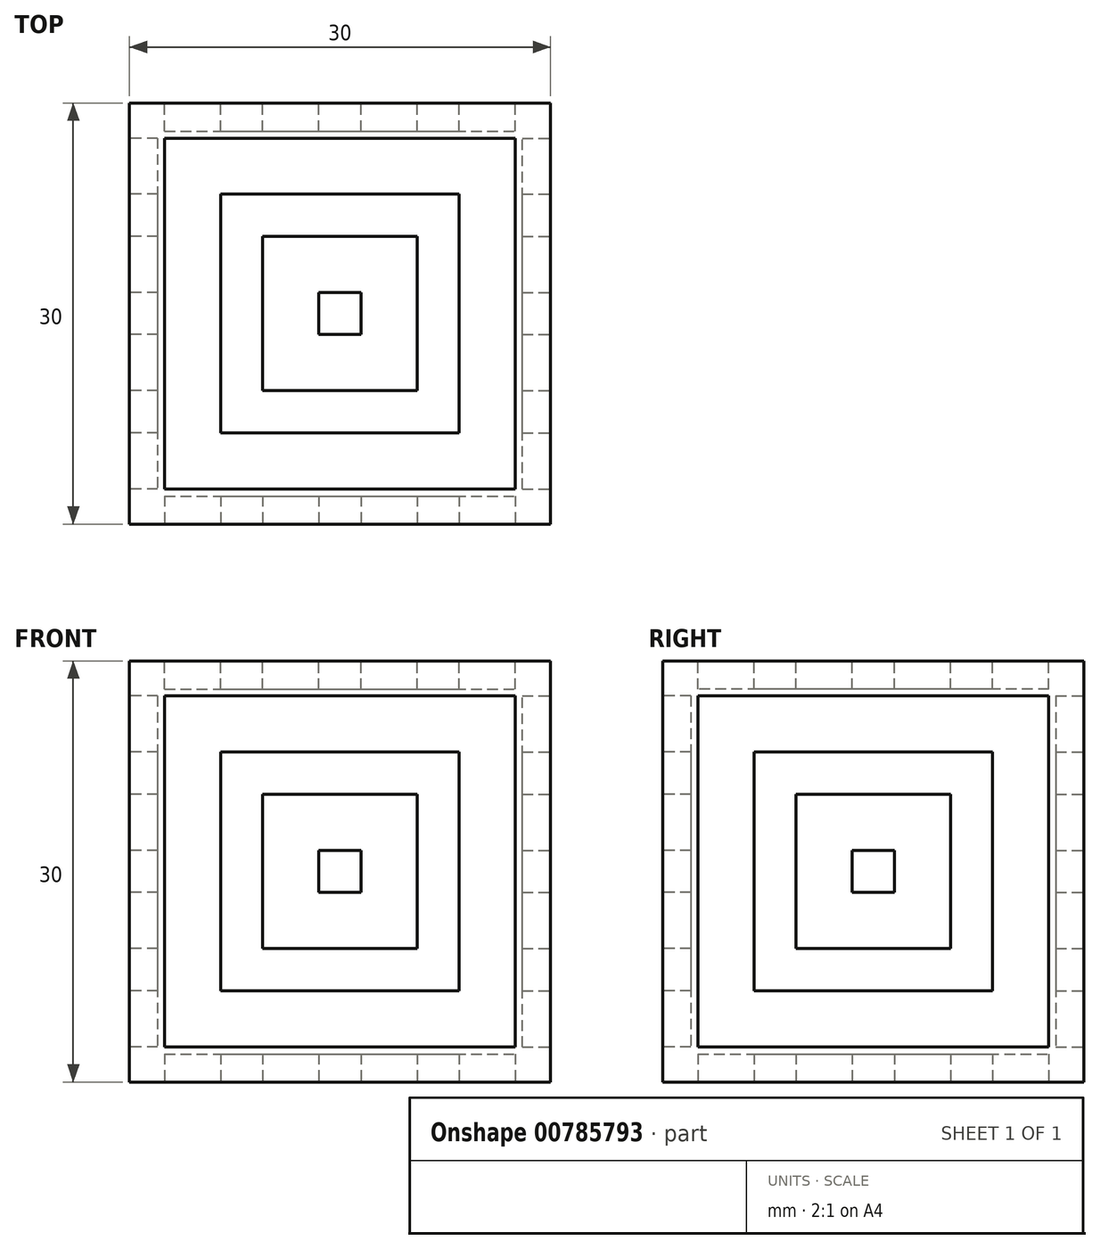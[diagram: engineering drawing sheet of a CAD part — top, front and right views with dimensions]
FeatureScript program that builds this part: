
annotation { "Feature Type Name" : "Feature", "Feature Type Description" : "" }
export const myFeature = defineFeature(function(context is Context, id is Id, definition is map)
    precondition{}
    {
        {
            var Q0;
            Q0=qCreatedBy(makeId("Front.planeOp"),FACE);
            var sketch = newSketch(context, id + "F0", { "sketchPlane" : qUnion([Q0])});
            skLineSegment(sketch, "E0.bottom", {"start": v(-15, 15) * mm, "end": v(15, 15) * mm});
            skLineSegment(sketch, "E0.top", {"start": v(-15, -15) * mm, "end": v(15, -15) * mm});
            skLineSegment(sketch, "E0.left", {"start": v(-15, 15) * mm, "end": v(-15, -15) * mm});
            skLineSegment(sketch, "E0.right", {"start": v(15, 15) * mm, "end": v(15, -15) * mm});
            skLineSegment(sketch, "E1", {"start": v(0, -15) * mm, "end": v(0, 15) * mm, "construction": true});
            skSolve(sketch);
        }
        {
            var Q0;
            Q0=makeQuery(id+"F0.imprint","IMPRINT",FACE,{"disambiguationData":[TD([[makeQuery(id+"F0.imprint","IMPRINT",EDGE,{"derivedFrom":sQuery(id+"F0.wireOp",EDGE,"E0.bottom")}),-1.0]])]});
            extrude(context, id + "F1", {"entities" : qUnion([Q0]), "depth" : 30 * mm, "offsetDistance" : 25 * mm});
        }
        {
            var Q0;
            Q0=makeQuery(id+"F1.opExtrude","SWEPT_FACE",FACE,{"disambiguationData":[OSD([sQuery(id+"F0.wireOp",EDGE,"E0.bottom")])]});
            var sketch = newSketch(context, id + "F2", { "sketchPlane" : qUnion([Q0])});
            skLineSegment(sketch, "E2", {"start": v(-15, -15) * mm, "end": v(15, -15) * mm, "construction": true});
            skLineSegment(sketch, "E3.bottom", {"start": v(-12.5, -2.5) * mm, "end": v(12.5, -2.5) * mm});
            skLineSegment(sketch, "E3.top", {"start": v(-12.5, -27.5) * mm, "end": v(12.5, -27.5) * mm});
            skLineSegment(sketch, "E3.left", {"start": v(-12.5, -2.5) * mm, "end": v(-12.5, -27.5) * mm});
            skLineSegment(sketch, "E3.right", {"start": v(12.5, -2.5) * mm, "end": v(12.5, -27.5) * mm});
            skLineSegment(sketch, "E4.bottom", {"start": v(-8.5, -6.5) * mm, "end": v(8.5, -6.5) * mm});
            skLineSegment(sketch, "E4.top", {"start": v(-8.5, -23.5) * mm, "end": v(8.5, -23.5) * mm});
            skLineSegment(sketch, "E4.left", {"start": v(-8.5, -6.5) * mm, "end": v(-8.5, -23.5) * mm});
            skLineSegment(sketch, "E4.right", {"start": v(8.5, -6.5) * mm, "end": v(8.5, -23.5) * mm});
            skLineSegment(sketch, "E5.bottom", {"start": v(-5.5, -9.5) * mm, "end": v(5.5, -9.5) * mm});
            skLineSegment(sketch, "E5.top", {"start": v(-5.5, -20.5) * mm, "end": v(5.5, -20.5) * mm});
            skLineSegment(sketch, "E5.left", {"start": v(-5.5, -9.5) * mm, "end": v(-5.5, -20.5) * mm});
            skLineSegment(sketch, "E5.right", {"start": v(5.5, -9.5) * mm, "end": v(5.5, -20.5) * mm});
            skLineSegment(sketch, "E6.bottom", {"start": v(-1.5, -13.5) * mm, "end": v(1.5, -13.5) * mm});
            skLineSegment(sketch, "E6.top", {"start": v(-1.5, -16.5) * mm, "end": v(1.5, -16.5) * mm});
            skLineSegment(sketch, "E6.left", {"start": v(-1.5, -13.5) * mm, "end": v(-1.5, -16.5) * mm});
            skLineSegment(sketch, "E6.right", {"start": v(1.5, -13.5) * mm, "end": v(1.5, -16.5) * mm});
            skSolve(sketch);
        }
        {
            var Q0;
            Q0=makeQuery(id+"F2.imprint","IMPRINT",FACE,{"disambiguationData":[TD([[makeQuery(id+"F2.imprint","IMPRINT",EDGE,{"derivedFrom":sQuery(id+"F2.wireOp",EDGE,"uRex6tDN-udSz-zSj9-Kkrf-qTBRgqxozcQJ.bottom")}),1.0]])]});
            var Q1;
            Q1=makeQuery(id+"F2.imprint","IMPRINT",FACE,{"disambiguationData":[TD([[makeQuery(id+"F2.imprint","IMPRINT",EDGE,{"derivedFrom":sQuery(id+"F2.wireOp",EDGE,"nGBAWDwn-kgTz-4052-Sxm5-BeoUUgHGIjmJ.bottom")}),1.0]])]});
            var Q2;
            Q2=makeQuery(id+"F2.imprint","IMPRINT",FACE,{"disambiguationData":[TD([[makeQuery(id+"F2.imprint","IMPRINT",EDGE,{"derivedFrom":sQuery(id+"F2.wireOp",EDGE,"Ts3vciQo-iaMk-j7SQ-Ruw9-omWsGh7XscNK.bottom")}),1.0]])]});
            var Q3;
            Q3=makeQuery(id+"F2.imprint","IMPRINT",FACE,{"disambiguationData":[TD([[makeQuery(id+"F2.imprint","IMPRINT",EDGE,{"derivedFrom":sQuery(id+"F2.wireOp",EDGE,"jwiH9sGp-5Auh-8KHc-ONIb-wjMNg3qUETeV.bottom")}),1.0]])]});
            var Q4;
            Q4=makeQuery(id+"F2.imprint","IMPRINT",FACE,{"disambiguationData":[TD([[makeQuery(id+"F2.imprint","IMPRINT",EDGE,{"derivedFrom":sQuery(id+"F2.wireOp",EDGE,"E3.bottom")}),-1.0]])]});
            var Q5;
            Q5=makeQuery(id+"F2.imprint","IMPRINT",FACE,{"disambiguationData":[TD([[makeQuery(id+"F2.imprint","IMPRINT",EDGE,{"derivedFrom":sQuery(id+"F2.wireOp",EDGE,"E5.bottom")}),-1.0]])]});
            extrude(context, id + "F3", {"entities" : qUnion([Q0, Q1, Q2, Q3, Q4, Q5]), "operationType" : NewBodyOperationType.REMOVE, "oppositeDirection" : true, "depth" : 2 * mm, "offsetDistance" : 25 * mm});
        }
        {
            var Q0;
            Q0=makeQuery(id+"F1.opExtrude","SWEPT_FACE",FACE,{"disambiguationData":[OSD([sQuery(id+"F0.wireOp",EDGE,"E0.left")])]});
            var sketch = newSketch(context, id + "F4", { "sketchPlane" : qUnion([Q0])});
            skLineSegment(sketch, "E7", {"start": v(15, 15) * mm, "end": v(15, -15) * mm, "construction": true});
            skLineSegment(sketch, "E8.bottom", {"start": v(2.5, 12.5) * mm, "end": v(27.5, 12.5) * mm});
            skLineSegment(sketch, "E8.top", {"start": v(2.5, -12.5) * mm, "end": v(27.5, -12.5) * mm});
            skLineSegment(sketch, "E8.left", {"start": v(2.5, 12.5) * mm, "end": v(2.5, -12.5) * mm});
            skLineSegment(sketch, "E8.right", {"start": v(27.5, 12.5) * mm, "end": v(27.5, -12.5) * mm});
            skLineSegment(sketch, "E9.bottom", {"start": v(6.5, 8.5) * mm, "end": v(23.5, 8.5) * mm});
            skLineSegment(sketch, "E9.top", {"start": v(6.5, -8.5) * mm, "end": v(23.5, -8.5) * mm});
            skLineSegment(sketch, "E9.left", {"start": v(6.5, 8.5) * mm, "end": v(6.5, -8.5) * mm});
            skLineSegment(sketch, "E9.right", {"start": v(23.5, 8.5) * mm, "end": v(23.5, -8.5) * mm});
            skLineSegment(sketch, "E10.bottom", {"start": v(9.5, 5.5) * mm, "end": v(20.5, 5.5) * mm});
            skLineSegment(sketch, "E10.top", {"start": v(9.5, -5.5) * mm, "end": v(20.5, -5.5) * mm});
            skLineSegment(sketch, "E10.left", {"start": v(9.5, 5.5) * mm, "end": v(9.5, -5.5) * mm});
            skLineSegment(sketch, "E10.right", {"start": v(20.5, 5.5) * mm, "end": v(20.5, -5.5) * mm});
            skLineSegment(sketch, "E11.bottom", {"start": v(13.5, 1.5) * mm, "end": v(16.5, 1.5) * mm});
            skLineSegment(sketch, "E11.top", {"start": v(13.5, -1.5) * mm, "end": v(16.5, -1.5) * mm});
            skLineSegment(sketch, "E11.left", {"start": v(13.5, 1.5) * mm, "end": v(13.5, -1.5) * mm});
            skLineSegment(sketch, "E11.right", {"start": v(16.5, 1.5) * mm, "end": v(16.5, -1.5) * mm});
            skSolve(sketch);
        }
        {
            var Q0;
            Q0=makeQuery(id+"F4.imprint","IMPRINT",FACE,{"disambiguationData":[TD([[makeQuery(id+"F4.imprint","IMPRINT",EDGE,{"derivedFrom":sQuery(id+"F4.wireOp",EDGE,"tFhn6pTz-PqA6-0Ceg-Cg85-YklQBv8rGbGZ.bottom")}),-1.0]])]});
            var Q1;
            Q1=makeQuery(id+"F4.imprint","IMPRINT",FACE,{"disambiguationData":[TD([[makeQuery(id+"F4.imprint","IMPRINT",EDGE,{"derivedFrom":sQuery(id+"F4.wireOp",EDGE,"VLWMtOgv-XsFV-Qeux-GhU2-IEdTUHNLQnk7.bottom")}),-1.0]])]});
            var Q2;
            Q2=makeQuery(id+"F4.imprint","IMPRINT",FACE,{"disambiguationData":[TD([[makeQuery(id+"F4.imprint","IMPRINT",EDGE,{"derivedFrom":sQuery(id+"F4.wireOp",EDGE,"xuadJEK9-1DuS-RCpM-Ft0Y-ZkX4oRwEia8Y.bottom")}),-1.0]])]});
            var Q3;
            Q3=makeQuery(id+"F4.imprint","IMPRINT",FACE,{"disambiguationData":[TD([[makeQuery(id+"F4.imprint","IMPRINT",EDGE,{"derivedFrom":sQuery(id+"F4.wireOp",EDGE,"h3vh0Wac-17uR-Dsb1-aqDi-2bTRFAljsAe5.bottom")}),-1.0]])]});
            var Q4;
            Q4=makeQuery(id+"F4.imprint","IMPRINT",FACE,{"disambiguationData":[TD([[makeQuery(id+"F4.imprint","IMPRINT",EDGE,{"derivedFrom":sQuery(id+"F4.wireOp",EDGE,"E8.bottom")}),-1.0]])]});
            var Q5;
            Q5=makeQuery(id+"F4.imprint","IMPRINT",FACE,{"disambiguationData":[TD([[makeQuery(id+"F4.imprint","IMPRINT",EDGE,{"derivedFrom":sQuery(id+"F4.wireOp",EDGE,"E10.bottom")}),-1.0]])]});
            extrude(context, id + "F5", {"entities" : qUnion([Q0, Q1, Q2, Q3, Q4, Q5]), "operationType" : NewBodyOperationType.REMOVE, "oppositeDirection" : true, "depth" : 2 * mm, "offsetDistance" : 25 * mm});
        }
        {
            var Q0;
            Q0=makeQuery(id+"F1.opExtrude","SWEPT_FACE",FACE,{"disambiguationData":[OSD([sQuery(id+"F0.wireOp",EDGE,"E0.top")])]});
            var sketch = newSketch(context, id + "F6", { "sketchPlane" : qUnion([Q0])});
            skLineSegment(sketch, "E12.left", {"start": v(-12.5, 27.5) * mm, "end": v(-12.5, 2.5) * mm});
            skLineSegment(sketch, "E13.right", {"start": v(12.5, 27.5) * mm, "end": v(12.5, 2.5) * mm});
            skLineSegment(sketch, "E14", {"start": v(-15, 15) * mm, "end": v(15, 15) * mm, "construction": true});
            skLineSegment(sketch, "E15", {"start": v(-12.5, 27.5) * mm, "end": v(12.5, 27.5) * mm});
            skLineSegment(sketch, "E16", {"start": v(-12.5, 2.5) * mm, "end": v(12.5, 2.5) * mm});
            skLineSegment(sketch, "E17.bottom", {"start": v(-8.5, 23.5) * mm, "end": v(8.5, 23.5) * mm});
            skLineSegment(sketch, "E17.top", {"start": v(-8.5, 6.5) * mm, "end": v(8.5, 6.5) * mm});
            skLineSegment(sketch, "E17.left", {"start": v(-8.5, 23.5) * mm, "end": v(-8.5, 6.5) * mm});
            skLineSegment(sketch, "E17.right", {"start": v(8.5, 23.5) * mm, "end": v(8.5, 6.5) * mm});
            skLineSegment(sketch, "E18.bottom", {"start": v(-5.5, 20.5) * mm, "end": v(5.5, 20.5) * mm});
            skLineSegment(sketch, "E18.top", {"start": v(-5.5, 9.5) * mm, "end": v(5.5, 9.5) * mm});
            skLineSegment(sketch, "E18.left", {"start": v(-5.5, 20.5) * mm, "end": v(-5.5, 9.5) * mm});
            skLineSegment(sketch, "E18.right", {"start": v(5.5, 20.5) * mm, "end": v(5.5, 9.5) * mm});
            skLineSegment(sketch, "E19.bottom", {"start": v(-1.5, 16.5) * mm, "end": v(1.5, 16.5) * mm});
            skLineSegment(sketch, "E19.top", {"start": v(-1.5, 13.5) * mm, "end": v(1.5, 13.5) * mm});
            skLineSegment(sketch, "E19.left", {"start": v(-1.5, 16.5) * mm, "end": v(-1.5, 13.5) * mm});
            skLineSegment(sketch, "E19.right", {"start": v(1.5, 16.5) * mm, "end": v(1.5, 13.5) * mm});
            skSolve(sketch);
        }
        {
            var Q0;
            Q0=makeQuery(id+"F6.imprint","IMPRINT",FACE,{"disambiguationData":[TD([[makeQuery(id+"F6.imprint","IMPRINT",EDGE,{"derivedFrom":sQuery(id+"F6.wireOp",EDGE,"E12.bottom")}),-1.0]])]});
            var Q1;
            Q1=makeQuery(id+"F6.imprint","IMPRINT",FACE,{"disambiguationData":[TD([[makeQuery(id+"F6.imprint","IMPRINT",EDGE,{"derivedFrom":sQuery(id+"F6.wireOp",EDGE,"9gzwvhWY-UftR-Z3a9-vf84-o9lvoVk9e7XM.bottom")}),-1.0]])]});
            var Q2;
            Q2=makeQuery(id+"F6.imprint","IMPRINT",FACE,{"disambiguationData":[TD([[makeQuery(id+"F6.imprint","IMPRINT",EDGE,{"derivedFrom":sQuery(id+"F6.wireOp",EDGE,"61DMOB89-fJZl-ldZf-jucY-mWSX6dTBA3PV.bottom")}),-1.0]])]});
            var Q3;
            Q3=makeQuery(id+"F6.imprint","IMPRINT",FACE,{"disambiguationData":[TD([[makeQuery(id+"F6.imprint","IMPRINT",EDGE,{"derivedFrom":sQuery(id+"F6.wireOp",EDGE,"E13.bottom")}),-1.0]])]});
            var Q4;
            Q4=makeQuery(id+"F6.imprint","IMPRINT",FACE,{"disambiguationData":[TD([[makeQuery(id+"F6.imprint","IMPRINT",EDGE,{"derivedFrom":sQuery(id+"F6.wireOp",EDGE,"E12.left")}),1.0]])]});
            var Q5;
            Q5=makeQuery(id+"F6.imprint","IMPRINT",FACE,{"disambiguationData":[TD([[makeQuery(id+"F6.imprint","IMPRINT",EDGE,{"derivedFrom":sQuery(id+"F6.wireOp",EDGE,"E18.bottom")}),-1.0]])]});
            extrude(context, id + "F7", {"entities" : qUnion([Q0, Q1, Q2, Q3, Q4, Q5]), "operationType" : NewBodyOperationType.REMOVE, "oppositeDirection" : true, "depth" : 2 * mm, "offsetDistance" : 25 * mm});
        }
        {
            var Q0;
            Q0=makeQuery(id+"F1.opExtrude","CAP_FACE",FACE,{"disambiguationData":[OSD([sQuery(id+"F0.wireOp",EDGE,"E0.bottom"),sQuery(id+"F0.wireOp",EDGE,"E0.top"),sQuery(id+"F0.wireOp",EDGE,"E0.left"),sQuery(id+"F0.wireOp",EDGE,"E0.right")])],"isStart":false});
            var sketch = newSketch(context, id + "F8", { "sketchPlane" : qUnion([Q0])});
            skLineSegment(sketch, "E20.left", {"start": v(-12.5, 12.5) * mm, "end": v(-12.5, -12.5) * mm});
            skLineSegment(sketch, "E21.right", {"start": v(12.5, 12.5) * mm, "end": v(12.5, -12.5) * mm});
            skLineSegment(sketch, "E22", {"start": v(-15, 0) * mm, "end": v(15, 0) * mm, "construction": true});
            skLineSegment(sketch, "E23", {"start": v(-12.5, 12.5) * mm, "end": v(12.5, 12.5) * mm});
            skLineSegment(sketch, "E24", {"start": v(-12.5, -12.5) * mm, "end": v(12.5, -12.5) * mm});
            skLineSegment(sketch, "E25", {"start": v(0, 15) * mm, "end": v(0, -15) * mm, "construction": true});
            skLineSegment(sketch, "E26.bottom", {"start": v(-8.5, 8.5) * mm, "end": v(8.5, 8.5) * mm});
            skLineSegment(sketch, "E26.top", {"start": v(-8.5, -8.5) * mm, "end": v(8.5, -8.5) * mm});
            skLineSegment(sketch, "E26.left", {"start": v(-8.5, 8.5) * mm, "end": v(-8.5, -8.5) * mm});
            skLineSegment(sketch, "E26.right", {"start": v(8.5, 8.5) * mm, "end": v(8.5, -8.5) * mm});
            skLineSegment(sketch, "E27.bottom", {"start": v(-5.5, 5.5) * mm, "end": v(5.5, 5.5) * mm});
            skLineSegment(sketch, "E27.top", {"start": v(-5.5, -5.5) * mm, "end": v(5.5, -5.5) * mm});
            skLineSegment(sketch, "E27.left", {"start": v(-5.5, 5.5) * mm, "end": v(-5.5, -5.5) * mm});
            skLineSegment(sketch, "E27.right", {"start": v(5.5, 5.5) * mm, "end": v(5.5, -5.5) * mm});
            skLineSegment(sketch, "E28.bottom", {"start": v(-1.5, 1.5) * mm, "end": v(1.5, 1.5) * mm});
            skLineSegment(sketch, "E28.top", {"start": v(-1.5, -1.5) * mm, "end": v(1.5, -1.5) * mm});
            skLineSegment(sketch, "E28.left", {"start": v(-1.5, 1.5) * mm, "end": v(-1.5, -1.5) * mm});
            skLineSegment(sketch, "E28.right", {"start": v(1.5, 1.5) * mm, "end": v(1.5, -1.5) * mm});
            skSolve(sketch);
        }
        {
            var Q0;
            Q0=makeQuery(id+"F8.imprint","IMPRINT",FACE,{"disambiguationData":[TD([[makeQuery(id+"F8.imprint","IMPRINT",EDGE,{"derivedFrom":sQuery(id+"F8.wireOp",EDGE,"E20.bottom")}),-1.0]])]});
            var Q1;
            Q1=makeQuery(id+"F8.imprint","IMPRINT",FACE,{"disambiguationData":[TD([[makeQuery(id+"F8.imprint","IMPRINT",EDGE,{"derivedFrom":sQuery(id+"F8.wireOp",EDGE,"w2OAYovl-fpUU-RyPA-OO3a-YtueSPJR6AJ7.bottom")}),-1.0]])]});
            var Q2;
            Q2=makeQuery(id+"F8.imprint","IMPRINT",FACE,{"disambiguationData":[TD([[makeQuery(id+"F8.imprint","IMPRINT",EDGE,{"derivedFrom":sQuery(id+"F8.wireOp",EDGE,"AbDRh6JB-hv8i-oSrv-NRIs-S1HOo0ejkXZN.bottom")}),-1.0]])]});
            var Q3;
            Q3=makeQuery(id+"F8.imprint","IMPRINT",FACE,{"disambiguationData":[TD([[makeQuery(id+"F8.imprint","IMPRINT",EDGE,{"derivedFrom":sQuery(id+"F8.wireOp",EDGE,"E21.bottom")}),-1.0]])]});
            var Q4;
            Q4=makeQuery(id+"F8.imprint","IMPRINT",FACE,{"disambiguationData":[TD([[makeQuery(id+"F8.imprint","IMPRINT",EDGE,{"derivedFrom":sQuery(id+"F8.wireOp",EDGE,"E20.left")}),1.0]])]});
            var Q5;
            Q5=makeQuery(id+"F8.imprint","IMPRINT",FACE,{"disambiguationData":[TD([[makeQuery(id+"F8.imprint","IMPRINT",EDGE,{"derivedFrom":sQuery(id+"F8.wireOp",EDGE,"E27.bottom")}),-1.0]])]});
            extrude(context, id + "F9", {"entities" : qUnion([Q0, Q1, Q2, Q3, Q4, Q5]), "operationType" : NewBodyOperationType.REMOVE, "oppositeDirection" : true, "depth" : 2 * mm, "offsetDistance" : 25 * mm});
        }
        {
            var Q0;
            Q0=makeQuery(id+"F1.opExtrude","CAP_FACE",FACE,{"disambiguationData":[OSD([sQuery(id+"F0.wireOp",EDGE,"E0.bottom"),sQuery(id+"F0.wireOp",EDGE,"E0.top"),sQuery(id+"F0.wireOp",EDGE,"E0.left"),sQuery(id+"F0.wireOp",EDGE,"E0.right")])],"isStart":true});
            var sketch = newSketch(context, id + "F10", { "sketchPlane" : qUnion([Q0])});
            skLineSegment(sketch, "E29", {"start": v(-15, 0) * mm, "end": v(15, 0) * mm, "construction": true});
            skLineSegment(sketch, "E30.bottom", {"start": v(12.5, 12.5) * mm, "end": v(-12.5, 12.5) * mm});
            skLineSegment(sketch, "E30.top", {"start": v(12.5, -12.5) * mm, "end": v(-12.5, -12.5) * mm});
            skLineSegment(sketch, "E30.left", {"start": v(12.5, 12.5) * mm, "end": v(12.5, -12.5) * mm});
            skLineSegment(sketch, "E30.right", {"start": v(-12.5, 12.5) * mm, "end": v(-12.5, -12.5) * mm});
            skLineSegment(sketch, "E31.bottom", {"start": v(8.5, 8.5) * mm, "end": v(-8.5, 8.5) * mm});
            skLineSegment(sketch, "E31.top", {"start": v(8.5, -8.5) * mm, "end": v(-8.5, -8.5) * mm});
            skLineSegment(sketch, "E31.left", {"start": v(8.5, 8.5) * mm, "end": v(8.5, -8.5) * mm});
            skLineSegment(sketch, "E31.right", {"start": v(-8.5, 8.5) * mm, "end": v(-8.5, -8.5) * mm});
            skLineSegment(sketch, "E32.bottom", {"start": v(5.5, 5.5) * mm, "end": v(-5.5, 5.5) * mm});
            skLineSegment(sketch, "E32.top", {"start": v(5.5, -5.5) * mm, "end": v(-5.5, -5.5) * mm});
            skLineSegment(sketch, "E32.left", {"start": v(5.5, 5.5) * mm, "end": v(5.5, -5.5) * mm});
            skLineSegment(sketch, "E32.right", {"start": v(-5.5, 5.5) * mm, "end": v(-5.5, -5.5) * mm});
            skLineSegment(sketch, "E33.bottom", {"start": v(1.5, 1.5) * mm, "end": v(-1.5, 1.5) * mm});
            skLineSegment(sketch, "E33.top", {"start": v(1.5, -1.5) * mm, "end": v(-1.5, -1.5) * mm});
            skLineSegment(sketch, "E33.left", {"start": v(1.5, 1.5) * mm, "end": v(1.5, -1.5) * mm});
            skLineSegment(sketch, "E33.right", {"start": v(-1.5, 1.5) * mm, "end": v(-1.5, -1.5) * mm});
            skSolve(sketch);
        }
        {
            var Q0;
            Q0=makeQuery(id+"F10.imprint","IMPRINT",FACE,{"disambiguationData":[TD([[makeQuery(id+"F10.imprint","IMPRINT",EDGE,{"derivedFrom":sQuery(id+"F10.wireOp",EDGE,"hQI7XaXH-FAcv-136m-JDHG-CGOvF3jEEl87.bottom")}),-1.0]])]});
            var Q1;
            Q1=makeQuery(id+"F10.imprint","IMPRINT",FACE,{"disambiguationData":[TD([[makeQuery(id+"F10.imprint","IMPRINT",EDGE,{"derivedFrom":sQuery(id+"F10.wireOp",EDGE,"rHD9H0XU-G0uY-gYGo-e7Wd-VP38nCkX5GB6.bottom")}),1.0]])]});
            var Q2;
            Q2=makeQuery(id+"F10.imprint","IMPRINT",FACE,{"disambiguationData":[TD([[makeQuery(id+"F10.imprint","IMPRINT",EDGE,{"derivedFrom":sQuery(id+"F10.wireOp",EDGE,"Hadi83Yw-kUgn-p36U-wnSj-bUMtidgGDgzL.bottom")}),-1.0]])]});
            var Q3;
            Q3=makeQuery(id+"F10.imprint","IMPRINT",FACE,{"disambiguationData":[TD([[makeQuery(id+"F10.imprint","IMPRINT",EDGE,{"derivedFrom":sQuery(id+"F10.wireOp",EDGE,"zGdVCPuh-qT1q-IaGu-zIGy-6kJY0rWJWrSV.bottom")}),-1.0]])]});
            var Q4;
            Q4=makeQuery(id+"F10.imprint","IMPRINT",FACE,{"disambiguationData":[TD([[makeQuery(id+"F10.imprint","IMPRINT",EDGE,{"derivedFrom":sQuery(id+"F10.wireOp",EDGE,"E30.bottom")}),1.0]])]});
            var Q5;
            Q5=makeQuery(id+"F10.imprint","IMPRINT",FACE,{"disambiguationData":[TD([[makeQuery(id+"F10.imprint","IMPRINT",EDGE,{"derivedFrom":sQuery(id+"F10.wireOp",EDGE,"E32.bottom")}),1.0]])]});
            extrude(context, id + "F11", {"entities" : qUnion([Q0, Q1, Q2, Q3, Q4, Q5]), "operationType" : NewBodyOperationType.REMOVE, "oppositeDirection" : true, "depth" : 2 * mm, "offsetDistance" : 25 * mm});
        }
        {
            var Q0;
            Q0=makeQuery(id+"F1.opExtrude","SWEPT_FACE",FACE,{"disambiguationData":[OSD([sQuery(id+"F0.wireOp",EDGE,"E0.right")])]});
            var sketch = newSketch(context, id + "F12", { "sketchPlane" : qUnion([Q0])});
            skLineSegment(sketch, "E34", {"start": v(-15, 15) * mm, "end": v(-15, -15) * mm, "construction": true});
            skLineSegment(sketch, "E35.bottom", {"start": v(-27.5, -12.5) * mm, "end": v(-2.5, -12.5) * mm});
            skLineSegment(sketch, "E35.top", {"start": v(-27.5, 12.5) * mm, "end": v(-2.5, 12.5) * mm});
            skLineSegment(sketch, "E35.left", {"start": v(-27.5, -12.5) * mm, "end": v(-27.5, 12.5) * mm});
            skLineSegment(sketch, "E35.right", {"start": v(-2.5, -12.5) * mm, "end": v(-2.5, 12.5) * mm});
            skLineSegment(sketch, "E36.bottom", {"start": v(-23.5, -8.5) * mm, "end": v(-6.5, -8.5) * mm});
            skLineSegment(sketch, "E36.top", {"start": v(-23.5, 8.5) * mm, "end": v(-6.5, 8.5) * mm});
            skLineSegment(sketch, "E36.left", {"start": v(-23.5, -8.5) * mm, "end": v(-23.5, 8.5) * mm});
            skLineSegment(sketch, "E36.right", {"start": v(-6.5, -8.5) * mm, "end": v(-6.5, 8.5) * mm});
            skLineSegment(sketch, "E37.bottom", {"start": v(-20.5, -5.5) * mm, "end": v(-9.5, -5.5) * mm});
            skLineSegment(sketch, "E37.top", {"start": v(-20.5, 5.5) * mm, "end": v(-9.5, 5.5) * mm});
            skLineSegment(sketch, "E37.left", {"start": v(-20.5, -5.5) * mm, "end": v(-20.5, 5.5) * mm});
            skLineSegment(sketch, "E37.right", {"start": v(-9.5, -5.5) * mm, "end": v(-9.5, 5.5) * mm});
            skLineSegment(sketch, "E38.bottom", {"start": v(-16.5, -1.5) * mm, "end": v(-13.5, -1.5) * mm});
            skLineSegment(sketch, "E38.top", {"start": v(-16.5, 1.5) * mm, "end": v(-13.5, 1.5) * mm});
            skLineSegment(sketch, "E38.left", {"start": v(-16.5, -1.5) * mm, "end": v(-16.5, 1.5) * mm});
            skLineSegment(sketch, "E38.right", {"start": v(-13.5, -1.5) * mm, "end": v(-13.5, 1.5) * mm});
            skSolve(sketch);
        }
        {
            var Q0;
            Q0=makeQuery(id+"F12.imprint","IMPRINT",FACE,{"disambiguationData":[TD([[makeQuery(id+"F12.imprint","IMPRINT",EDGE,{"derivedFrom":sQuery(id+"F12.wireOp",EDGE,"hTRp0tKR-rDhT-8sIK-C4eh-JNg9UNseJaBx.bottom")}),-1.0]])]});
            var Q1;
            Q1=makeQuery(id+"F12.imprint","IMPRINT",FACE,{"disambiguationData":[TD([[makeQuery(id+"F12.imprint","IMPRINT",EDGE,{"derivedFrom":sQuery(id+"F12.wireOp",EDGE,"zhRrIRKS-WT5Z-qSos-q5G1-38y1dAa3Mi3s.bottom")}),-1.0]])]});
            var Q2;
            Q2=makeQuery(id+"F12.imprint","IMPRINT",FACE,{"disambiguationData":[TD([[makeQuery(id+"F12.imprint","IMPRINT",EDGE,{"derivedFrom":sQuery(id+"F12.wireOp",EDGE,"cH0rxdoh-gybH-e1KN-5kaz-pAEDsfxVMlh5.bottom")}),-1.0]])]});
            var Q3;
            Q3=makeQuery(id+"F12.imprint","IMPRINT",FACE,{"disambiguationData":[TD([[makeQuery(id+"F12.imprint","IMPRINT",EDGE,{"derivedFrom":sQuery(id+"F12.wireOp",EDGE,"WWbBiupg-0sQQ-PL8k-E3qh-14ZDVjTRICin.bottom")}),-1.0]])]});
            var Q4;
            Q4=makeQuery(id+"F12.imprint","IMPRINT",FACE,{"disambiguationData":[TD([[makeQuery(id+"F12.imprint","IMPRINT",EDGE,{"derivedFrom":sQuery(id+"F12.wireOp",EDGE,"E35.bottom")}),1.0]])]});
            var Q5;
            Q5=makeQuery(id+"F12.imprint","IMPRINT",FACE,{"disambiguationData":[TD([[makeQuery(id+"F12.imprint","IMPRINT",EDGE,{"derivedFrom":sQuery(id+"F12.wireOp",EDGE,"E37.bottom")}),1.0]])]});
            extrude(context, id + "F13", {"entities" : qUnion([Q0, Q1, Q2, Q3, Q4, Q5]), "operationType" : NewBodyOperationType.REMOVE, "oppositeDirection" : true, "depth" : 2 * mm, "offsetDistance" : 25 * mm});
        }
    });
